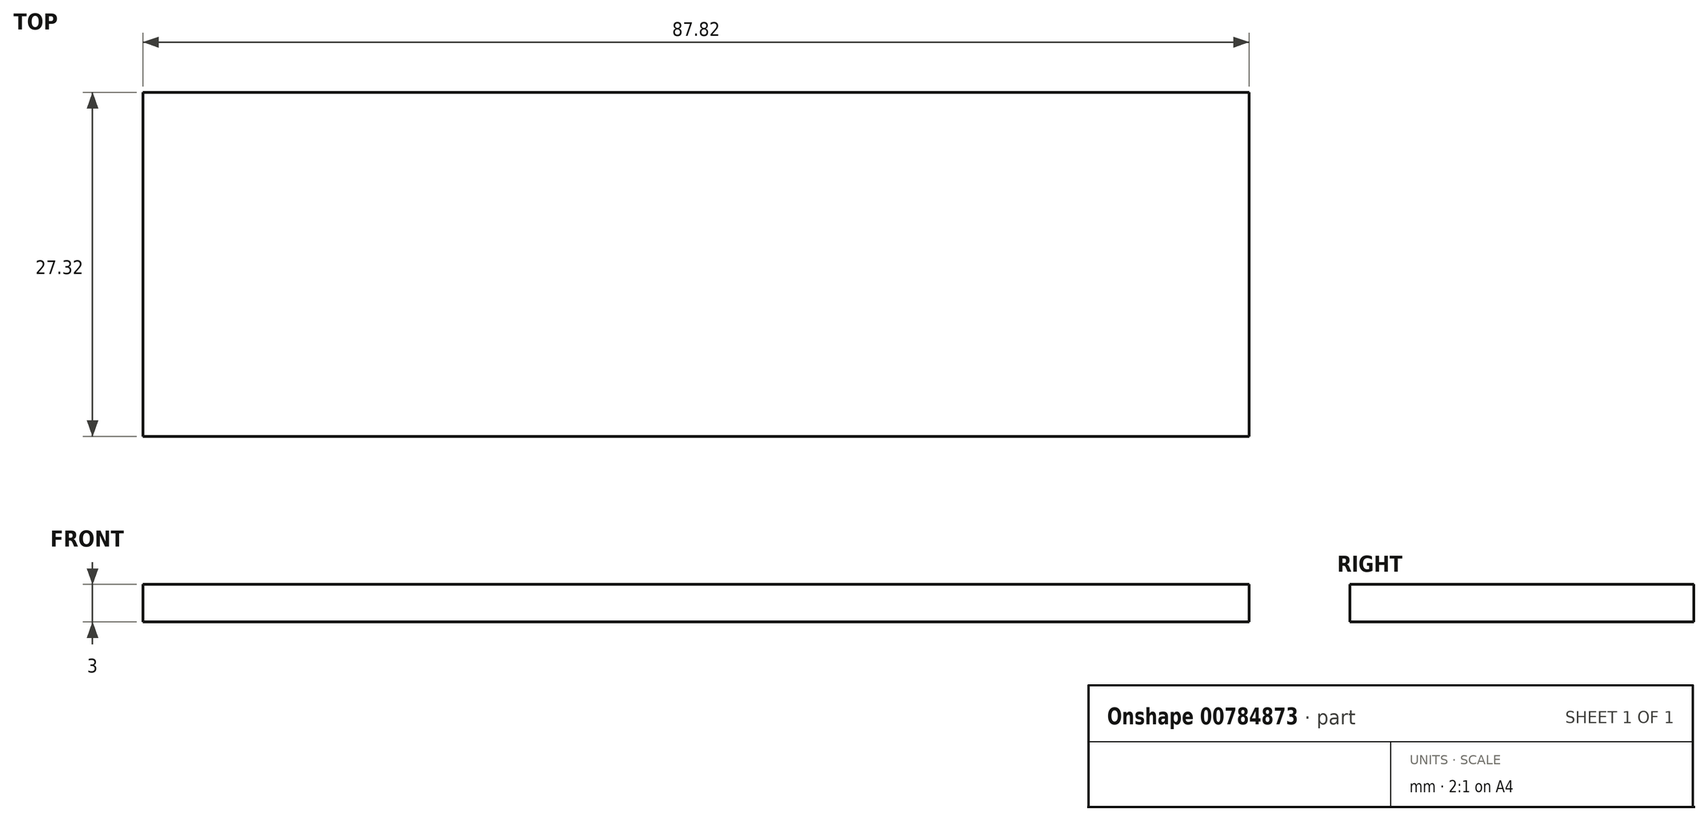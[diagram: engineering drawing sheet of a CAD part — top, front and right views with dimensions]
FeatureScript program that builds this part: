
annotation { "Feature Type Name" : "Feature", "Feature Type Description" : "" }
export const myFeature = defineFeature(function(context is Context, id is Id, definition is map)
    precondition{}
    {
        {
            var Q0;
            Q0=qCreatedBy(makeId("Top.planeOp"),FACE);
            var sketch = newSketch(context, id + "F0", { "sketchPlane" : qUnion([Q0])});
            skLineSegment(sketch, "E0.bottom", {"start": v(-43.9, -13.66) * mm, "end": v(43.9, -13.66) * mm});
            skLineSegment(sketch, "E0.top", {"start": v(-43.9, 13.66) * mm, "end": v(43.9, 13.66) * mm});
            skLineSegment(sketch, "E0.left", {"start": v(-43.9, -13.66) * mm, "end": v(-43.9, 13.66) * mm});
            skLineSegment(sketch, "E0.right", {"start": v(43.9, -13.66) * mm, "end": v(43.9, 13.66) * mm});
            skPoint(sketch, "E0.middle", {"position": v(0, 0) * mm});
            skSolve(sketch);
        }
        {
            var Q0;
            Q0=makeQuery(id+"F0.imprint","IMPRINT",FACE,{"disambiguationData":[TD([[makeQuery(id+"F0.imprint","IMPRINT",EDGE,{"derivedFrom":sQuery(id+"F0.wireOp",EDGE,"E0.bottom")}),1.0]])]});
            extrude(context, id + "F1", {"entities" : qUnion([Q0]), "depth" : 3 * mm, "offsetDistance" : 25 * mm});
        }
    });
